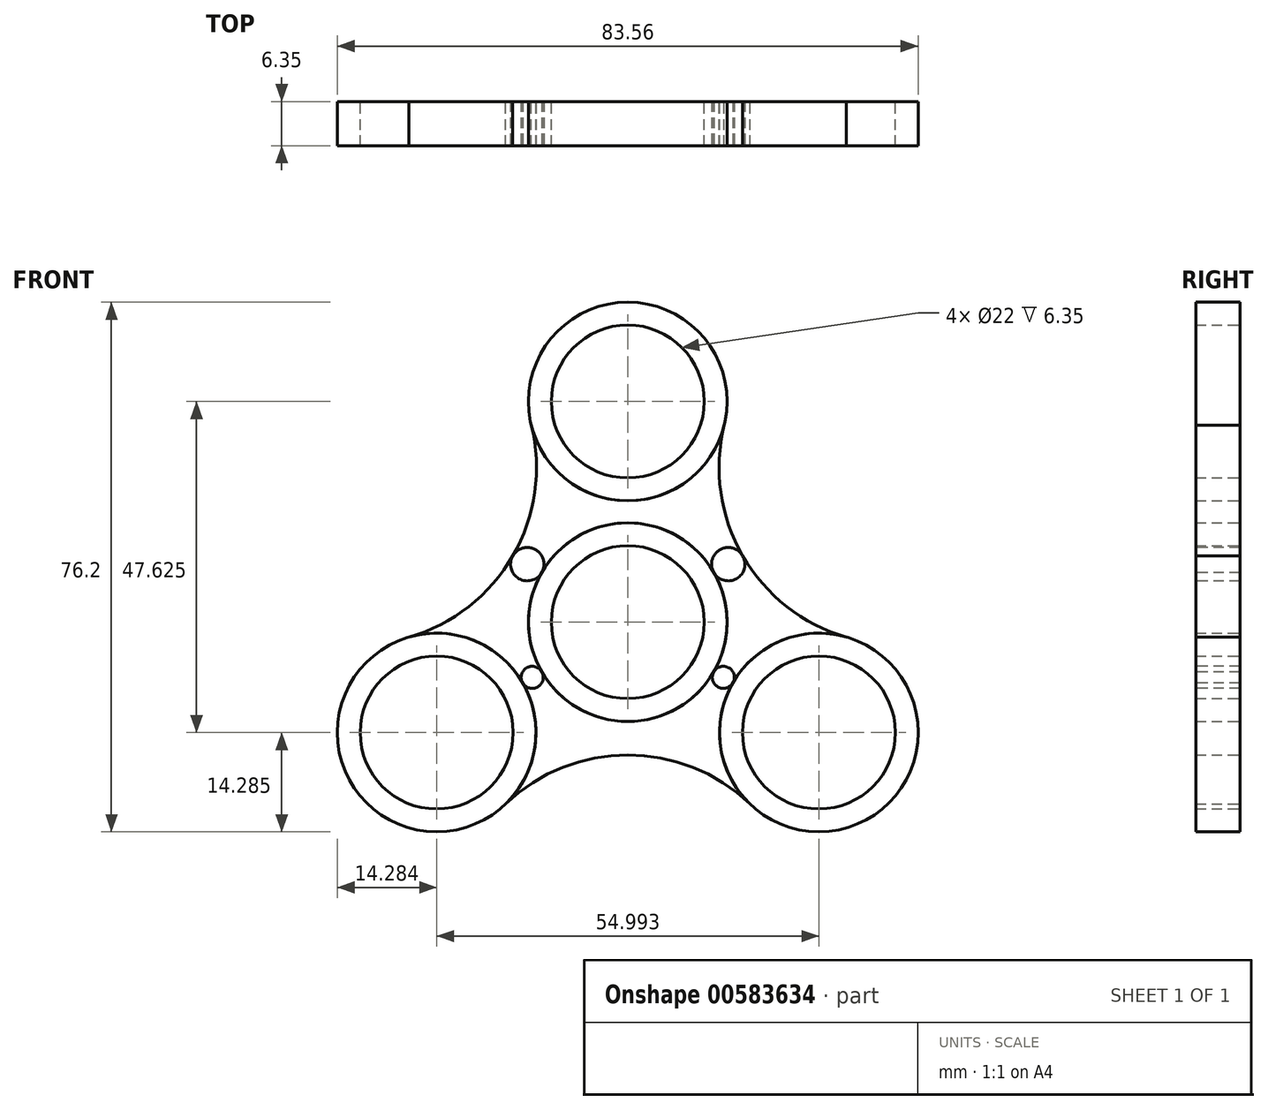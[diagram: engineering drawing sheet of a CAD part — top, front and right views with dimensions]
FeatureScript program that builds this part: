
annotation { "Feature Type Name" : "Feature", "Feature Type Description" : "" }
export const myFeature = defineFeature(function(context is Context, id is Id, definition is map)
    precondition{}
    {
        {
            var Q0;
            Q0=qCreatedBy(makeId("Front.planeOp"),FACE);
            var sketch = newSketch(context, id + "F0", { "sketchPlane" : qUnion([Q0])});
            skCircle(sketch, "E0", {"center": v(0, 0) * mm, "radius": 14.29 * mm});
            skCircle(sketch, "E1", {"center": v(0, 0) * mm, "radius": 11 * mm});
            skCircle(sketch, "E2", {"center": v(0, 31.75) * mm, "radius": 14.29 * mm});
            skCircle(sketch, "E3", {"center": v(0, 31.75) * mm, "radius": 11 * mm});
            skCircle(sketch, "E4.1.0", {"center": v(-27.5, -15.87) * mm, "radius": 14.29 * mm});
            skCircle(sketch, "E4.2.0", {"center": v(27.5, -15.88) * mm, "radius": 14.29 * mm});
            skCircle(sketch, "E5.1.0", {"center": v(-27.5, -15.87) * mm, "radius": 11 * mm});
            skCircle(sketch, "E5.2.0", {"center": v(27.5, -15.88) * mm, "radius": 11 * mm});
            skSolve(sketch);
        }
        {
            var Q0;
            Q0=qCreatedBy(makeId("Front.planeOp"),FACE);
            var sketch = newSketch(context, id + "F1", { "sketchPlane" : qUnion([Q0])});
            skCircle(sketch, "E6.0", {"center": v(0, 31.75) * mm, "radius": 14.29 * mm});
            skCircle(sketch, "E7.0", {"center": v(-27.5, -15.87) * mm, "radius": 14.29 * mm});
            skCircle(sketch, "E8.0", {"center": v(27.5, -15.88) * mm, "radius": 14.29 * mm});
            skCircle(sketch, "E9.0", {"center": v(0, 0) * mm, "radius": 11 * mm});
            skCircle(sketch, "E10.0", {"center": v(0, 0) * mm, "radius": 14.29 * mm});
            skCircle(sketch, "E11.0", {"center": v(0, 31.75) * mm, "radius": 11 * mm});
            skArc(sketch, "E12", {"start": v(-31.47, -2.15) * mm, "mid": v(-16.54, 9.55) * mm, "end": v(-13.87, 28.33) * mm});
            skArc(sketch, "E13", {"start": v(13.87, 28.33) * mm, "mid": v(16.54, 9.55) * mm, "end": v(31.47, -2.15) * mm});
            skArc(sketch, "E14", {"start": v(17.6, -26.18) * mm, "mid": v(0, -19.1) * mm, "end": v(-17.6, -26.18) * mm});
            skSolve(sketch);
        }
        {
            var Q0;
            Q0=makeQuery(id+"F1.imprint","IMPRINT",FACE,{"disambiguationData":[TD([[makeQuery(id+"F1.imprint","IMPRINT",EDGE,{"derivedFrom":sQuery(id+"F1.wireOp",EDGE,"E10.0")}),-1.0]])]});
            var Q1;
            Q1=makeQuery(id+"F0.imprint","IMPRINT",FACE,{"disambiguationData":[TD([[makeQuery(id+"F0.imprint","IMPRINT",EDGE,{"derivedFrom":sQuery(id+"F0.wireOp",EDGE,"E2")}),1.0]])]});
            var Q2;
            Q2=makeQuery(id+"F0.imprint","IMPRINT",FACE,{"disambiguationData":[TD([[makeQuery(id+"F0.imprint","IMPRINT",EDGE,{"derivedFrom":sQuery(id+"F0.wireOp",EDGE,"E4.1.0")}),1.0]])]});
            var Q3;
            Q3=makeQuery(id+"F0.imprint","IMPRINT",FACE,{"disambiguationData":[TD([[makeQuery(id+"F0.imprint","IMPRINT",EDGE,{"derivedFrom":sQuery(id+"F0.wireOp",EDGE,"E4.2.0")}),1.0]])]});
            var Q4;
            Q4=makeQuery(id+"F0.imprint","IMPRINT",FACE,{"disambiguationData":[TD([[makeQuery(id+"F0.imprint","IMPRINT",EDGE,{"derivedFrom":sQuery(id+"F0.wireOp",EDGE,"E0")}),1.0]])]});
            extrude(context, id + "F2", {"entities" : qUnion([Q0, Q1, Q2, Q3, Q4]), "depth" : 6.35 * mm, "offsetDistance" : 25.4 * mm});
        }
        {
            var Q0;
            Q0=makeQuery(id+"F2.opExtrude","CAP_FACE",FACE,{"disambiguationData":[OSD([sQuery(id+"F1.wireOp",EDGE,"E6.0"),sQuery(id+"F1.wireOp",EDGE,"E7.0"),sQuery(id+"F1.wireOp",EDGE,"E8.0"),sQuery(id+"F1.wireOp",EDGE,"E10.0"),sQuery(id+"F1.wireOp",EDGE,"E12"),sQuery(id+"F1.wireOp",EDGE,"E13"),sQuery(id+"F1.wireOp",EDGE,"E14")])],"isStart":false});
            var sketch = newSketch(context, id + "F3", { "sketchPlane" : qUnion([Q0])});
            skText(sketch, "E15", { "text": "M", "fontName": "OpenSans-Bold.ttf"});
            skArc(sketch, "E16.0", {"start": v(-31.47, -2.15) * mm, "mid": v(-16.54, 9.55) * mm, "end": v(-13.87, 28.33) * mm});
            skCircle(sketch, "E17.0", {"center": v(0, 0) * mm, "radius": 14.29 * mm});
            skText(sketch, "E18", { "text": "M", "fontName": "OpenSans-Bold.ttf"});
            const initialGuessF3  = {"E15": [-0.01313, 0.01337, 1, 0, 0.00635], "E18": [0.00504, 0.01337, 1, 0, 0.00635]};
            skSetInitialGuess(sketch, initialGuessF3);
            skSolve(sketch);
        }
        {
            var Q0;
            Q0=makeQuery(id+"F3.imprint","IMPRINT",FACE,{"disambiguationData":[TD([[makeQuery(id+"F3.imprint","IMPRINT",EDGE,{"derivedFrom":sQuery(id+"F3.wireOp",EDGE,"E15.sketch_text.stroke-0")}),1.0]])]});
            var sketch = newSketch(context, id + "F4", { "sketchPlane" : qUnion([Q0])});
            skArc(sketch, "E19.0", {"start": v(-31.47, -2.15) * mm, "mid": v(-16.54, 9.55) * mm, "end": v(-13.87, 28.33) * mm});
            skText(sketch, "E20", { "text": "MANEY", "fontName": "OpenSans-Bold.ttf"});
            const initialGuessF4  = {"E20": [-0.0098, -0.0185, 1, 0, 0.00381]};
            skSetInitialGuess(sketch, initialGuessF4);
            skSolve(sketch);
        }
        {
            var Q0;
            Q0=makeQuery(id+"F3.imprint","IMPRINT",FACE,{"disambiguationData":[TD([[makeQuery(id+"F3.imprint","IMPRINT",EDGE,{"derivedFrom":sQuery(id+"F3.wireOp",EDGE,"E15.sketch_text.stroke-0")}),1.0]])]});
            var sketch = newSketch(context, id + "F5", { "sketchPlane" : qUnion([Q0])});
            skCircle(sketch, "E21", {"center": v(14.45, 8.35) * mm, "radius": 2.4 * mm});
            skCircle(sketch, "E22", {"center": v(-14.45, 8.35) * mm, "radius": 2.4 * mm});
            skSolve(sketch);
        }
        {
            var Q0;
            {var subQ0=sQuery(id+"F5.wireOp",EDGE,"E22");var subQ1=makeQuery(id+"F5.imprint","INTERSECT",VERTEX,{"derivedFrom":[makeQuery(id+"F3.imprint","IMPRINT",EDGE,{"derivedFrom":sQuery(id+"F3.wireOp",EDGE,"E16.0")}),subQ0]});Q0=makeQuery(id+"F5.imprint","IMPRINT",FACE,{"disambiguationData":[TD([[makeQuery(id+"F5.imprint","IMPRINT",EDGE,{"disambiguationData":[TD([[subQ1,-1.0]])],"derivedFrom":subQ0}),1.0]])]});}
            var Q1;
            {var subQ0=sQuery(id+"F5.wireOp",EDGE,"E21");var subQ1=makeQuery(id+"F5.imprint","INTERSECT",VERTEX,{"derivedFrom":[makeQuery(id+"F3.imprint","IMPRINT",EDGE,{"derivedFrom":makeQuery(id+"F2.opExtrude","CAP_EDGE",EDGE,{"disambiguationData":[OSD([sQuery(id+"F1.wireOp",EDGE,"E13")])],"isStart":false})}),subQ0]});Q1=makeQuery(id+"F5.imprint","IMPRINT",FACE,{"disambiguationData":[TD([[makeQuery(id+"F5.imprint","IMPRINT",EDGE,{"disambiguationData":[TD([[subQ1,-1.0]])],"derivedFrom":subQ0}),1.0]])]});}
            extrude(context, id + "F6", {"entities" : qUnion([Q0, Q1]), "operationType" : NewBodyOperationType.REMOVE, "oppositeDirection" : true, "depth" : 25.4 * mm, "offsetDistance" : 25.4 * mm});
        }
        {
            var Q0;
            Q0=makeQuery(id+"F3.imprint","IMPRINT",FACE,{"disambiguationData":[TD([[makeQuery(id+"F3.imprint","IMPRINT",EDGE,{"derivedFrom":sQuery(id+"F3.wireOp",EDGE,"E15.sketch_text.stroke-0")}),1.0]])]});
            var sketch = newSketch(context, id + "F7", { "sketchPlane" : qUnion([Q0])});
            skCircle(sketch, "E23", {"center": v(13.75, -7.94) * mm, "radius": 1.59 * mm});
            skCircle(sketch, "E24", {"center": v(-13.75, -7.94) * mm, "radius": 1.59 * mm});
            skSolve(sketch);
        }
        {
            var Q0;
            {var subQ0=sQuery(id+"F7.wireOp",EDGE,"E24");var subQ1=makeQuery(id+"F7.imprint","INTERSECT",VERTEX,{"derivedFrom":[makeQuery(id+"F3.imprint","IMPRINT",EDGE,{"derivedFrom":makeQuery(id+"F2.opExtrude","CAP_EDGE",EDGE,{"disambiguationData":[OSD([sQuery(id+"F1.wireOp",EDGE,"E7.0")])],"isStart":false})}),subQ0]});Q0=makeQuery(id+"F7.imprint","IMPRINT",FACE,{"disambiguationData":[TD([[makeQuery(id+"F7.imprint","IMPRINT",EDGE,{"disambiguationData":[TD([[subQ1,1.0]])],"derivedFrom":subQ0}),1.0]])]});}
            var Q1;
            {var subQ0=sQuery(id+"F7.wireOp",EDGE,"E23");var subQ1=makeQuery(id+"F7.imprint","INTERSECT",VERTEX,{"derivedFrom":[makeQuery(id+"F3.imprint","IMPRINT",EDGE,{"derivedFrom":makeQuery(id+"F2.opExtrude","CAP_EDGE",EDGE,{"disambiguationData":[OSD([sQuery(id+"F1.wireOp",EDGE,"E8.0")])],"isStart":false})}),subQ0]});Q1=makeQuery(id+"F7.imprint","IMPRINT",FACE,{"disambiguationData":[TD([[makeQuery(id+"F7.imprint","IMPRINT",EDGE,{"disambiguationData":[TD([[subQ1,1.0]])],"derivedFrom":subQ0}),1.0]])]});}
            extrude(context, id + "F8", {"entities" : qUnion([Q0, Q1]), "operationType" : NewBodyOperationType.REMOVE, "oppositeDirection" : true, "depth" : 25.4 * mm, "offsetDistance" : 25.4 * mm});
        }
    });
